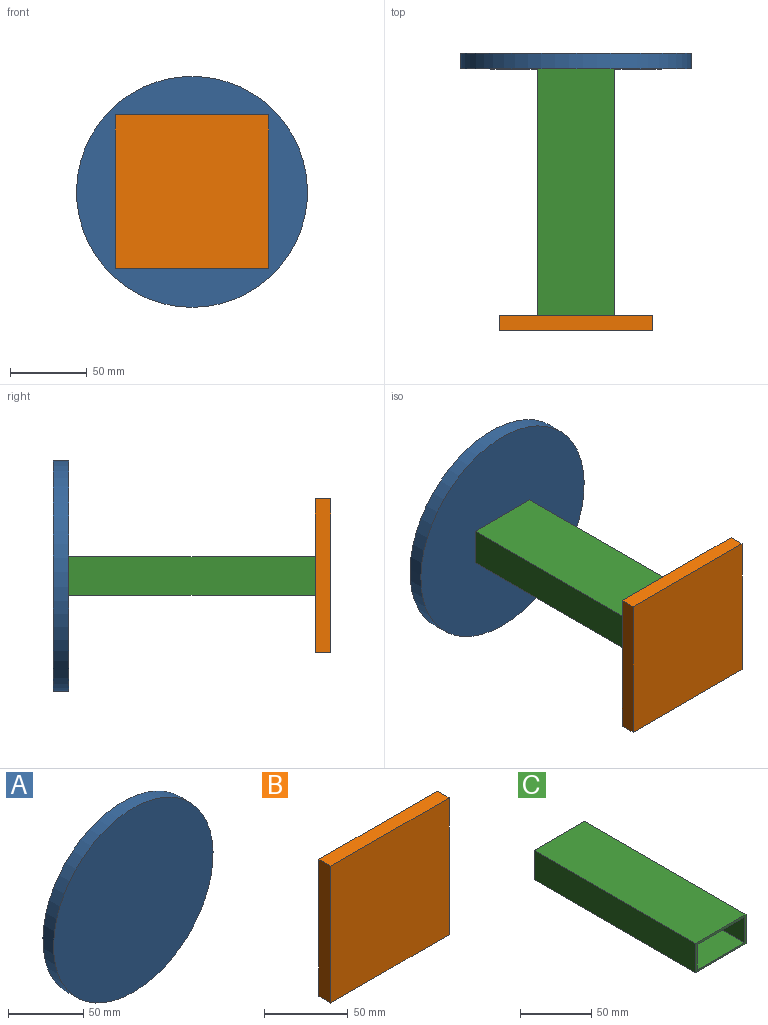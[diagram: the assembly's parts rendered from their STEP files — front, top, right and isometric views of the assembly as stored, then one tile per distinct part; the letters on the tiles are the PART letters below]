
ASSEMBLY  parts=3 mates=2
PART A: 3 faces, bbox 150x10x150 mm
  f0: cylinder r=75mm len=150mm, axis (0,1,0), area 4712.4mm2, adj f1,f2
  f1: plane 150x150mm, normal (0,-1,0), area 17671.5mm2, adj f0
  f2: plane 150x150mm, normal (0,1,0), area 17671.5mm2, adj f0
PART B: 6 faces, bbox 100x10x100 mm
  f0: plane 100x10mm, normal (0,0,1), area 1000mm2, adj f1,f3,f4,f5
  f1: plane 100x10mm, normal (-1,0,0), area 1000mm2, adj f0,f2,f4,f5
  f2: plane 100x10mm, normal (0,0,-1), area 1000mm2, adj f1,f3,f4,f5
  f3: plane 100x10mm, normal (1,0,0), area 1000mm2, adj f0,f2,f4,f5
  f4: plane 100x100mm, normal (0,-1,0), area 10000mm2, adj f0,f1,f2,f3
  f5: plane 100x100mm, normal (0,1,0), area 10000mm2, adj f0,f1,f2,f3
PART C: 10 faces, bbox 50x160x25 mm
  f0: plane 160x50mm, normal (0,0,1), area 8000mm2, adj f1,f7,f8,f9
  f1: plane 160x25mm, normal (-1,0,0), area 4000mm2, adj f0,f2,f8,f9
  f2: plane 160x50mm, normal (0,0,-1), area 8000mm2, adj f1,f7,f8,f9
  f3: plane 160x22mm, normal (1,0,0), area 3520mm2, adj f4,f6,f8,f9
  f4: plane 160x47mm, normal (0,0,-1), area 7520mm2, adj f3,f5,f8,f9
  f5: plane 160x22mm, normal (-1,0,0), area 3520mm2, adj f4,f6,f8,f9
  f6: plane 160x47mm, normal (0,0,1), area 7520mm2, adj f3,f5,f8,f9
  f7: plane 160x25mm, normal (1,0,0), area 4000mm2, adj f0,f2,f8,f9
  f8: plane 50x25mm, normal (0,-1,0), area 216mm2, adj f0,f1,f2,f3,f4,f5,f6,f7
  f9: plane 50x25mm, normal (0,1,0), area 216mm2, adj f0,f1,f2,f3,f4,f5,f6,f7
PLACE A t=(0,85,0)mm
PLACE B t=(0,-85,0)mm
PLACE C at identity
MATE fastened B.f5 <-> C.f8  axis (0,1,0) through (0,-80,0)mm
MATE fastened A.f0 <-> C.f9  axis (0,-1,0) through (0,80,0)mm
